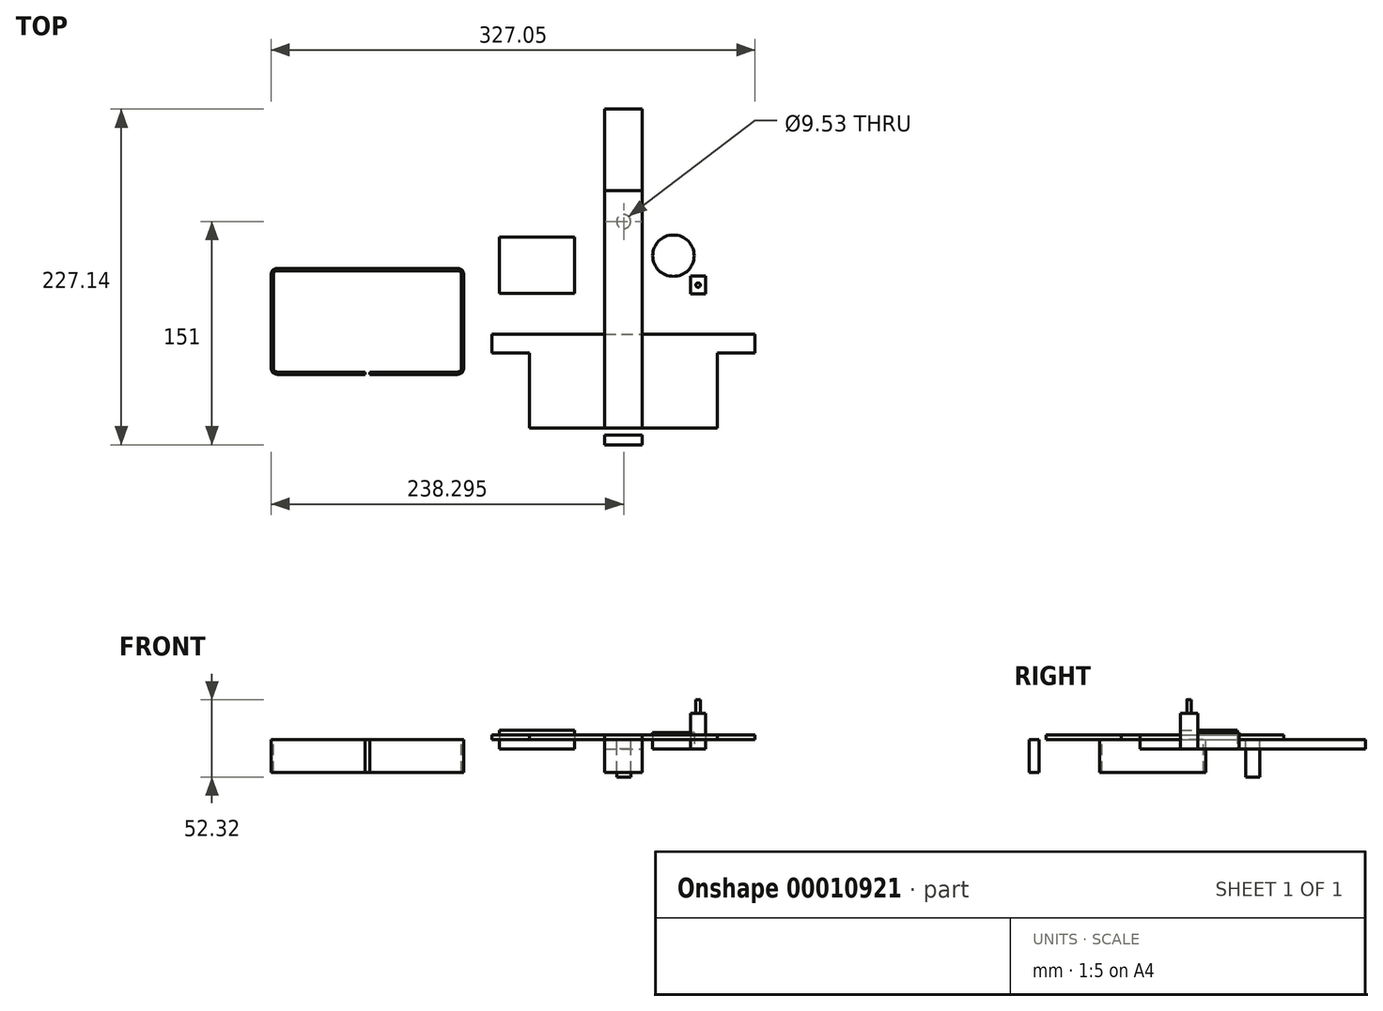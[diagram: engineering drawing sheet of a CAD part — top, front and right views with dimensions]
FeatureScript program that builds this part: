
annotation { "Feature Type Name" : "Feature", "Feature Type Description" : "" }
export const myFeature = defineFeature(function(context is Context, id is Id, definition is map)
    precondition{}
    {
        {
            var Q0;
            Q0=qCreatedBy(makeId("Top.planeOp"),FACE);
            var sketch = newSketch(context, id + "F0", { "sketchPlane" : qUnion([Q0])});
            skLineSegment(sketch, "E0.bottom", {"start": v(0, 0) * mm, "end": v(25.4, 0) * mm});
            skLineSegment(sketch, "E0.top", {"start": v(0, 152.4) * mm, "end": v(25.4, 152.4) * mm});
            skLineSegment(sketch, "E0.left", {"start": v(0, 0) * mm, "end": v(0, 152.4) * mm});
            skLineSegment(sketch, "E0.right", {"start": v(25.4, 0) * mm, "end": v(25.4, 152.4) * mm});
            skSolve(sketch);
        }
        {
            var Q0;
            Q0 = qSketchRegion(id + "F0", true);
            extrude(context, id + "F1", {"entities" : qUnion([Q0]), "depth" : 6.35 * mm});
        }
        {
            var Q0;
            Q0=makeQuery(id+"F1.opExtrude","CAP_FACE",FACE,{"disambiguationData":[OSD([sQuery(id+"F0.wireOp",EDGE,"E0.bottom"),sQuery(id+"F0.wireOp",EDGE,"E0.top"),sQuery(id+"F0.wireOp",EDGE,"E0.left"),sQuery(id+"F0.wireOp",EDGE,"E0.right")])],"isStart":false});
            var sketch = newSketch(context, id + "F2", { "sketchPlane" : qUnion([Q0])});
            skCircle(sketch, "E1", {"center": v(12.85, 76.26) * mm, "radius": 4.76 * mm});
            skSolve(sketch);
        }
        {
            var Q0;
            Q0 = qSketchRegion(id + "F2", true);
            extrude(context, id + "F3", {"entities" : qUnion([Q0]), "operationType" : NewBodyOperationType.REMOVE, "endBound" : BoundingType.THROUGH_ALL, "oppositeDirection" : true, "depth" : 25.4 * mm});
        }
        {
            var Q0;
            Q0=makeQuery(id+"F1.opExtrude","CAP_FACE",FACE,{"disambiguationData":[OSD([sQuery(id+"F0.wireOp",EDGE,"E0.bottom"),sQuery(id+"F0.wireOp",EDGE,"E0.top"),sQuery(id+"F0.wireOp",EDGE,"E0.left"),sQuery(id+"F0.wireOp",EDGE,"E0.right")])],"isStart":false});
            var sketch = newSketch(context, id + "F4", { "sketchPlane" : qUnion([Q0])});
            skLineSegment(sketch, "E2.bottom", {"start": v(0, 97.35) * mm, "end": v(25.24, 97.35) * mm});
            skLineSegment(sketch, "E3.0.MirrorCS", {"start": v(-50.8, 0) * mm, "end": v(-50.8, -63.5) * mm});
            skLineSegment(sketch, "E4", {"start": v(-50.8, -63.5) * mm, "end": v(12.7, -63.5) * mm});
            skLineSegment(sketch, "E5", {"start": v(25.4, 0) * mm, "end": v(25.24, 97.35) * mm});
            skLineSegment(sketch, "E6", {"start": v(0, 97.35) * mm, "end": v(0, 0) * mm});
            skLineSegment(sketch, "E7", {"start": v(0, 0) * mm, "end": v(-50.8, 0) * mm});
            skLineSegment(sketch, "E8", {"start": v(12.7, 0) * mm, "end": v(12.7, -63.5) * mm});
            skLineSegment(sketch, "E9.0.MirrorCS", {"start": v(76.2, -63.5) * mm, "end": v(12.7, -63.5) * mm});
            skLineSegment(sketch, "E10.0.MirrorCS", {"start": v(76.2, 0) * mm, "end": v(76.2, -63.5) * mm});
            skLineSegment(sketch, "E11.0.MirrorCS", {"start": v(25.4, 0) * mm, "end": v(76.2, 0) * mm});
            skLineSegment(sketch, "E12.bottom", {"start": v(-50.8, 0) * mm, "end": v(-76.2, 0) * mm});
            skLineSegment(sketch, "E12.top", {"start": v(-50.8, -12.7) * mm, "end": v(-76.2, -12.7) * mm});
            skLineSegment(sketch, "E12.left", {"start": v(-50.8, 0) * mm, "end": v(-50.8, -12.7) * mm});
            skLineSegment(sketch, "E12.right", {"start": v(-76.2, 0) * mm, "end": v(-76.2, -12.7) * mm});
            skLineSegment(sketch, "E13.0.MirrorCS", {"start": v(76.2, -12.7) * mm, "end": v(101.6, -12.7) * mm});
            skLineSegment(sketch, "E14.0.MirrorCS", {"start": v(101.6, 0) * mm, "end": v(101.6, -12.7) * mm});
            skLineSegment(sketch, "E15.0.MirrorCS", {"start": v(76.2, 0) * mm, "end": v(101.6, 0) * mm});
            skSolve(sketch);
        }
        {
            var Q0;
            Q0 = qSketchRegion(id + "F4", true);
            extrude(context, id + "F5", {"entities" : qUnion([Q0]), "depth" : 3.17 * mm});
        }
        {
            var Q0;
            Q0=qCreatedBy(makeId("Top.planeOp"),FACE);
            var sketch = newSketch(context, id + "F6", { "sketchPlane" : qUnion([Q0])});
            skLineSegment(sketch, "E16.bottom", {"start": v(58.2, 27.3) * mm, "end": v(68.2, 27.3) * mm});
            skLineSegment(sketch, "E16.top", {"start": v(58.2, 39.3) * mm, "end": v(68.2, 39.3) * mm});
            skLineSegment(sketch, "E16.left", {"start": v(58.2, 27.3) * mm, "end": v(58.2, 39.3) * mm});
            skLineSegment(sketch, "E16.right", {"start": v(68.2, 27.3) * mm, "end": v(68.2, 39.3) * mm});
            skSolve(sketch);
        }
        {
            var Q0;
            Q0 = qSketchRegion(id + "F6", true);
            extrude(context, id + "F7", {"entities" : qUnion([Q0]), "depth" : 24 * mm});
        }
        {
            var Q0;
            Q0=makeQuery(id+"F7.opExtrude","CAP_FACE",FACE,{"disambiguationData":[OSD([sQuery(id+"F6.wireOp",EDGE,"E16.bottom"),sQuery(id+"F6.wireOp",EDGE,"E16.top"),sQuery(id+"F6.wireOp",EDGE,"E16.left"),sQuery(id+"F6.wireOp",EDGE,"E16.right")])],"isStart":false});
            var sketch = newSketch(context, id + "F8", { "sketchPlane" : qUnion([Q0])});
            skLineSegment(sketch, "E17", {"start": v(68.2, 33.3) * mm, "end": v(58.2, 33.3) * mm});
            skCircle(sketch, "E18", {"center": v(63.2, 33.3) * mm, "radius": 1.5 * mm});
            skSolve(sketch);
        }
        {
            var Q0;
            Q0 = qSketchRegion(id + "F8", true);
            extrude(context, id + "F9", {"entities" : qUnion([Q0]), "operationType" : NewBodyOperationType.ADD, "depth" : 9.27 * mm});
        }
        {
            var Q0;
            Q0=qCreatedBy(makeId("Top.planeOp"),FACE);
            var sketch = newSketch(context, id + "F10", { "sketchPlane" : qUnion([Q0])});
            skLineSegment(sketch, "E19.bottom", {"start": v(-71.27, 27.67) * mm, "end": v(-20.47, 27.67) * mm});
            skLineSegment(sketch, "E19.top", {"start": v(-71.27, 65.77) * mm, "end": v(-20.47, 65.77) * mm});
            skLineSegment(sketch, "E19.left", {"start": v(-71.27, 27.67) * mm, "end": v(-71.27, 65.77) * mm});
            skLineSegment(sketch, "E19.right", {"start": v(-20.47, 27.67) * mm, "end": v(-20.47, 65.77) * mm});
            skSolve(sketch);
        }
        {
            var Q0;
            Q0 = qSketchRegion(id + "F10", true);
            extrude(context, id + "F11", {"entities" : qUnion([Q0]), "depth" : 12.7 * mm});
        }
        {
            var Q0;
            Q0=qCreatedBy(makeId("Top.planeOp"),FACE);
            var sketch = newSketch(context, id + "F12", { "sketchPlane" : qUnion([Q0])});
            skCircle(sketch, "E20", {"center": v(46.5, 53.2) * mm, "radius": 14 * mm});
            skSolve(sketch);
        }
        {
            var Q0;
            Q0 = qSketchRegion(id + "F12", true);
            extrude(context, id + "F13", {"entities" : qUnion([Q0]), "depth" : 11 * mm});
        }
        {
            var Q0;
            Q0=makeQuery(id+"F5.opExtrude","CAP_FACE",FACE,{"disambiguationData":[OSD([sQuery(id+"F4.wireOp",EDGE,"E2.bottom"),sQuery(id+"F4.wireOp",EDGE,"E3.0.MirrorCS"),sQuery(id+"F4.wireOp",EDGE,"E4"),sQuery(id+"F4.wireOp",EDGE,"E5"),sQuery(id+"F4.wireOp",EDGE,"E6"),sQuery(id+"F4.wireOp",EDGE,"E7"),sQuery(id+"F4.wireOp",EDGE,"E9.0.MirrorCS"),sQuery(id+"F4.wireOp",EDGE,"E10.0.MirrorCS"),sQuery(id+"F4.wireOp",EDGE,"E11.0.MirrorCS"),sQuery(id+"F4.wireOp",EDGE,"E12.bottom"),sQuery(id+"F4.wireOp",EDGE,"E12.top"),sQuery(id+"F4.wireOp",EDGE,"E12.right"),sQuery(id+"F4.wireOp",EDGE,"E13.0.MirrorCS"),sQuery(id+"F4.wireOp",EDGE,"E14.0.MirrorCS"),sQuery(id+"F4.wireOp",EDGE,"E15.0.MirrorCS")])],"isStart":true});
            var sketch = newSketch(context, id + "F14", { "sketchPlane" : qUnion([Q0])});
            skCircle(sketch, "E21.0", {"center": v(12.85, -76.26) * mm, "radius": 4.76 * mm});
            skSolve(sketch);
        }
        {
            var Q0;
            Q0 = qSketchRegion(id + "F14", true);
            extrude(context, id + "F15", {"entities" : qUnion([Q0]), "depth" : 25.4 * mm});
        }
        {
            var Q0;
            Q0=makeQuery(id+"F5.opExtrude","CAP_FACE",FACE,{"disambiguationData":[OSD([sQuery(id+"F4.wireOp",EDGE,"E2.bottom"),sQuery(id+"F4.wireOp",EDGE,"E3.0.MirrorCS"),sQuery(id+"F4.wireOp",EDGE,"E4"),sQuery(id+"F4.wireOp",EDGE,"E5"),sQuery(id+"F4.wireOp",EDGE,"E6"),sQuery(id+"F4.wireOp",EDGE,"E7"),sQuery(id+"F4.wireOp",EDGE,"E9.0.MirrorCS"),sQuery(id+"F4.wireOp",EDGE,"E10.0.MirrorCS"),sQuery(id+"F4.wireOp",EDGE,"E11.0.MirrorCS"),sQuery(id+"F4.wireOp",EDGE,"E12.bottom"),sQuery(id+"F4.wireOp",EDGE,"E12.top"),sQuery(id+"F4.wireOp",EDGE,"E12.right"),sQuery(id+"F4.wireOp",EDGE,"E13.0.MirrorCS"),sQuery(id+"F4.wireOp",EDGE,"E14.0.MirrorCS"),sQuery(id+"F4.wireOp",EDGE,"E15.0.MirrorCS")])],"isStart":true});
            var sketch = newSketch(context, id + "F16", { "sketchPlane" : qUnion([Q0])});
            skLineSegment(sketch, "E22", {"start": v(-221.33, 25.52) * mm, "end": v(-99.4, 25.52) * mm});
            skArc(sketch, "E23.2", {"start": v(-95.28, 22.98) * mm, "mid": v(-96.49, 25.9) * mm, "end": v(-99.4, 27.1) * mm});
            skPoint(sketch, "E24.visualSharp", {"position": v(-96.87, 25.52) * mm});
            skLineSegment(sketch, "E25", {"start": v(-96.87, 22.98) * mm, "end": v(-96.87, -40.52) * mm});
            skLineSegment(sketch, "E26", {"start": v(-99.4, -43.06) * mm, "end": v(-221.33, -43.06) * mm});
            skLineSegment(sketch, "E23.6", {"start": v(-225.45, -40.52) * mm, "end": v(-225.45, 22.98) * mm});
            skLineSegment(sketch, "E23.3", {"start": v(-221.33, 27.1) * mm, "end": v(-99.4, 27.1) * mm});
            skPoint(sketch, "E27.visualSharp", {"position": v(-223.87, 25.52) * mm});
            skLineSegment(sketch, "E23.5", {"start": v(-99.4, -44.65) * mm, "end": v(-221.33, -44.65) * mm});
            skPoint(sketch, "E28.visualSharp", {"position": v(-96.87, -43.06) * mm});
            skPoint(sketch, "E29.visualSharp", {"position": v(-223.87, -43.06) * mm});
            skLineSegment(sketch, "E30", {"start": v(-223.87, -40.52) * mm, "end": v(-223.87, 22.98) * mm});
            skLineSegment(sketch, "E23.1", {"start": v(-95.28, 22.98) * mm, "end": v(-95.28, -40.52) * mm});
            skArc(sketch, "E23.7", {"start": v(-225.45, -40.52) * mm, "mid": v(-224.25, -43.44) * mm, "end": v(-221.33, -44.65) * mm});
            skArc(sketch, "E23.4", {"start": v(-221.33, 27.1) * mm, "mid": v(-224.25, 25.9) * mm, "end": v(-225.45, 22.98) * mm});
            skArc(sketch, "E23.0", {"start": v(-99.4, -44.65) * mm, "mid": v(-96.49, -43.44) * mm, "end": v(-95.28, -40.52) * mm});
            skArc(sketch, "E28.filletArc", {"start": v(-99.4, -43.06) * mm, "mid": v(-97.61, -42.32) * mm, "end": v(-96.87, -40.52) * mm});
            skArc(sketch, "E29.filletArc", {"start": v(-223.87, -40.52) * mm, "mid": v(-223.12, -42.32) * mm, "end": v(-221.33, -43.06) * mm});
            skArc(sketch, "E24.filletArc", {"start": v(-96.87, 22.98) * mm, "mid": v(-97.61, 24.78) * mm, "end": v(-99.4, 25.52) * mm});
            skArc(sketch, "E27.filletArc", {"start": v(-221.33, 25.52) * mm, "mid": v(-223.12, 24.78) * mm, "end": v(-223.87, 22.98) * mm});
            skSolve(sketch);
        }
        {
            var Q0;
            Q0 = qSketchRegion(id + "F16", true);
            extrude(context, id + "F17", {"entities" : qUnion([Q0]), "depth" : 22.22 * mm});
        }
        {
            var Q0;
            Q0=makeQuery(id+"F5.opExtrude","CAP_FACE",FACE,{"disambiguationData":[OSD([sQuery(id+"F4.wireOp",EDGE,"E2.bottom"),sQuery(id+"F4.wireOp",EDGE,"E3.0.MirrorCS"),sQuery(id+"F4.wireOp",EDGE,"E4"),sQuery(id+"F4.wireOp",EDGE,"E5"),sQuery(id+"F4.wireOp",EDGE,"E6"),sQuery(id+"F4.wireOp",EDGE,"E7"),sQuery(id+"F4.wireOp",EDGE,"E9.0.MirrorCS"),sQuery(id+"F4.wireOp",EDGE,"E10.0.MirrorCS"),sQuery(id+"F4.wireOp",EDGE,"E11.0.MirrorCS"),sQuery(id+"F4.wireOp",EDGE,"E12.bottom"),sQuery(id+"F4.wireOp",EDGE,"E12.top"),sQuery(id+"F4.wireOp",EDGE,"E12.right"),sQuery(id+"F4.wireOp",EDGE,"E13.0.MirrorCS"),sQuery(id+"F4.wireOp",EDGE,"E14.0.MirrorCS"),sQuery(id+"F4.wireOp",EDGE,"E15.0.MirrorCS")])],"isStart":true});
            var sketch = newSketch(context, id + "F18", { "sketchPlane" : qUnion([Q0])});
            skLineSegment(sketch, "E31", {"start": v(0, -97.35) * mm, "end": v(0, 63.5) * mm});
            skLineSegment(sketch, "E32", {"start": v(0, 63.5) * mm, "end": v(25.4, 63.5) * mm});
            skLineSegment(sketch, "E33", {"start": v(25.4, 63.5) * mm, "end": v(25.24, -97.35) * mm});
            skLineSegment(sketch, "E34", {"start": v(25.24, -97.35) * mm, "end": v(0, -97.35) * mm});
            skLineSegment(sketch, "E35", {"start": v(0, -97.35) * mm, "end": v(0, 0) * mm});
            skSolve(sketch);
        }
        {
            var Q0;
            Q0 = qSketchRegion(id + "F18", true);
            extrude(context, id + "F19", {"entities" : qUnion([Q0]), "oppositeDirection" : true, "depth" : 3.17 * mm});
        }
        {
            var Q0;
            Q0=makeQuery(id+"F19.opExtrude","CAP_FACE",FACE,{"disambiguationData":[OSD([sQuery(id+"F18.wireOp",EDGE,"E31"),sQuery(id+"F18.wireOp",EDGE,"E32"),sQuery(id+"F18.wireOp",EDGE,"E33"),sQuery(id+"F18.wireOp",EDGE,"E34"),sQuery(id+"F18.wireOp",EDGE,"E35")])],"isStart":true});
            var sketch = newSketch(context, id + "F20", { "sketchPlane" : qUnion([Q0])});
            skLineSegment(sketch, "E36.bottom", {"start": v(25.41, 74.74) * mm, "end": v(0, 74.74) * mm});
            skLineSegment(sketch, "E36.top", {"start": v(25.41, 68.24) * mm, "end": v(0, 68.24) * mm});
            skLineSegment(sketch, "E36.left", {"start": v(25.41, 74.74) * mm, "end": v(25.41, 68.24) * mm});
            skLineSegment(sketch, "E36.right", {"start": v(0, 74.74) * mm, "end": v(0, 68.24) * mm});
            skSolve(sketch);
        }
        {
            var Q0;
            Q0 = qSketchRegion(id + "F20", true);
            extrude(context, id + "F21", {"entities" : qUnion([Q0]), "depth" : 22.22 * mm});
        }
        {
            var Q0;
            Q0=makeQuery(id+"F17.opExtrude","SWEPT_FACE",FACE,{"disambiguationData":[OSD([sQuery(id+"F16.wireOp",EDGE,"E23.3")])]});
            var sketch = newSketch(context, id + "F22", { "sketchPlane" : qUnion([Q0])});
            skLineSegment(sketch, "E37.bottom", {"start": v(-160.37, 6.35) * mm, "end": v(-158.78, 6.35) * mm});
            skLineSegment(sketch, "E37.top", {"start": v(-160.37, -15.88) * mm, "end": v(-158.78, -15.88) * mm});
            skLineSegment(sketch, "E37.right", {"start": v(-158.78, 6.35) * mm, "end": v(-158.78, -15.88) * mm});
            skLineSegment(sketch, "E38.0.MirrorCS", {"start": v(-160.37, 6.35) * mm, "end": v(-161.95, 6.35) * mm});
            skLineSegment(sketch, "E39.0.MirrorCS", {"start": v(-161.95, 6.35) * mm, "end": v(-161.95, -15.88) * mm});
            skLineSegment(sketch, "E40.0.MirrorCS", {"start": v(-160.37, -15.88) * mm, "end": v(-161.95, -15.88) * mm});
            skSolve(sketch);
        }
        {
            var Q0;
            Q0 = qSketchRegion(id + "F22", true);
            var Q1;
            Q1=makeQuery(id+"F17.opExtrude","SWEPT_FACE",FACE,{"disambiguationData":[OSD([sQuery(id+"F16.wireOp",EDGE,"E22")])]});
            extrude(context, id + "F23", {"entities" : qUnion([Q0]), "operationType" : NewBodyOperationType.REMOVE, "endBound" : BoundingType.UP_TO_SURFACE, "oppositeDirection" : true, "endBoundEntityFace" : qUnion([Q1]), "depth" : 25.4 * mm});
        }
    });
